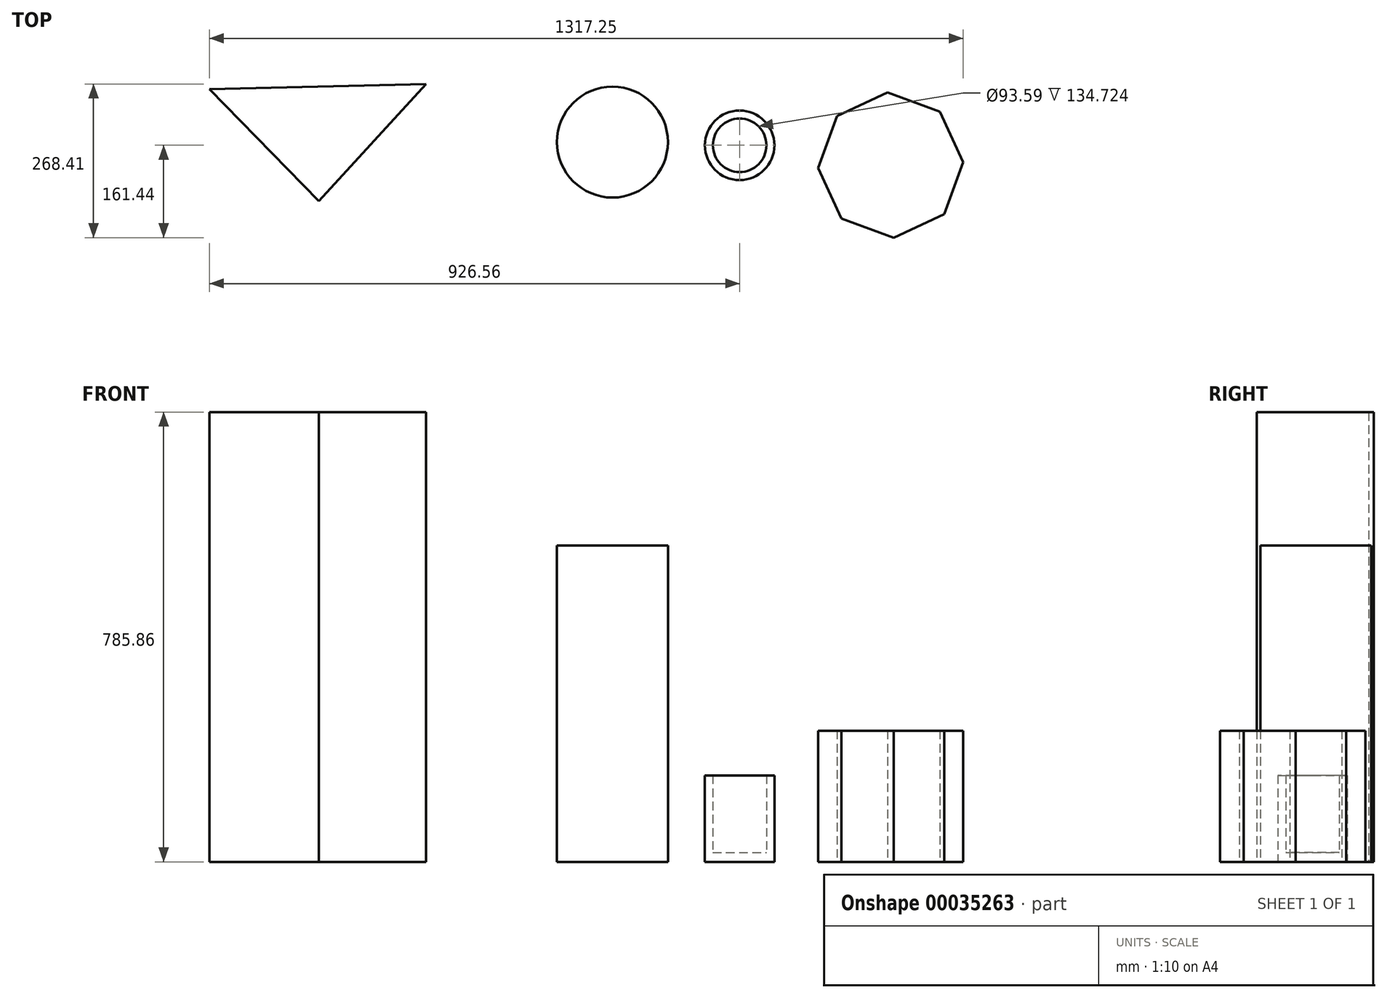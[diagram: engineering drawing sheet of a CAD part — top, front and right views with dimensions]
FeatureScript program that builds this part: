
annotation { "Feature Type Name" : "Feature", "Feature Type Description" : "" }
export const myFeature = defineFeature(function(context is Context, id is Id, definition is map)
    precondition{}
    {
        {
            var Q0;
            Q0=qCreatedBy(makeId("Front.planeOp"),FACE);
            var sketch = newSketch(context, id + "F0", { "sketchPlane" : qUnion([Q0])});
            skLineSegment(sketch, "E0.bottom", {"start": v(0, 0) * mm, "end": v(60.7, 0) * mm});
            skLineSegment(sketch, "E0.top", {"start": v(0, 16.33) * mm, "end": v(60.7, 16.33) * mm});
            skLineSegment(sketch, "E0.left", {"start": v(0, 0) * mm, "end": v(0, 16.33) * mm});
            skLineSegment(sketch, "E0.right", {"start": v(60.7, 0) * mm, "end": v(60.7, 16.33) * mm});
            skLineSegment(sketch, "E1.bottom", {"start": v(60.7, 0) * mm, "end": v(46.8, 0) * mm});
            skLineSegment(sketch, "E1.top", {"start": v(60.7, 151.05) * mm, "end": v(46.8, 151.05) * mm});
            skLineSegment(sketch, "E1.left", {"start": v(60.7, 0) * mm, "end": v(60.7, 151.05) * mm});
            skLineSegment(sketch, "E1.right", {"start": v(46.8, 0) * mm, "end": v(46.8, 151.05) * mm});
            skLineSegment(sketch, "E2", {"start": v(0, 0) * mm, "end": v(0, 193.86) * mm, "construction": true});
            skSolve(sketch);
        }
        {
            var Q0;
            {var subQ5=sQuery(id+"F0.wireOp",EDGE,"E1.top");Q0=makeQuery(id+"F0.imprint","IMPRINT",FACE,{"disambiguationData":[TD([[makeQuery(id+"F0.imprint","IMPRINT",EDGE,{"derivedFrom":subQ5}),1.0]])]});}
            var Q1;
            {var subQ5=sQuery(id+"F0.wireOp",EDGE,"E1.bottom");Q1=makeQuery(id+"F0.imprint","IMPRINT",FACE,{"disambiguationData":[TD([[makeQuery(id+"F0.imprint","IMPRINT",EDGE,{"derivedFrom":subQ5}),-1.0]])]});}
            var Q2;
            {var subQ0=sQuery(id+"F0.wireOp",EDGE,"E0.bottom");Q2=makeQuery(id+"F0.imprint","IMPRINT",FACE,{"disambiguationData":[TD([[makeQuery(id+"F0.imprint","IMPRINT",EDGE,{"derivedFrom":subQ0}),1.0]])]});}
            var Q3;
            Q3=sQuery(id+"F0.wireOp",EDGE,"E2");
            revolve(context, id + "F1", {"entities" : qUnion([Q0, Q1, Q2]), "axis" : qUnion([Q3]), "revolveType" : RevolveType.FULL});
        }
        {
            var Q0;
            Q0=qCreatedBy(makeId("Top.planeOp"),FACE);
            var sketch = newSketch(context, id + "F6", { "sketchPlane" : qUnion([Q0])});
            skCircle(sketch, "E3.cCircle", {"center": v(263.86, -34.6) * mm, "radius": 117.28 * mm, "construction": true});
            skLineSegment(sketch, "E3.0", {"start": v(390.7, -29.3) * mm, "end": v(357.28, -120.55) * mm});
            skLineSegment(sketch, "E3.1", {"start": v(357.28, -120.55) * mm, "end": v(269.15, -161.44) * mm});
            skLineSegment(sketch, "E3.2", {"start": v(269.15, -161.44) * mm, "end": v(177.91, -128.03) * mm});
            skLineSegment(sketch, "E3.3", {"start": v(177.91, -128.03) * mm, "end": v(137.02, -39.9) * mm});
            skLineSegment(sketch, "E3.4", {"start": v(137.02, -39.9) * mm, "end": v(170.43, 51.34) * mm});
            skLineSegment(sketch, "E3.5", {"start": v(170.43, 51.34) * mm, "end": v(258.56, 92.24) * mm});
            skLineSegment(sketch, "E3.6", {"start": v(258.56, 92.24) * mm, "end": v(349.8, 58.83) * mm});
            skLineSegment(sketch, "E3.7", {"start": v(349.8, 58.83) * mm, "end": v(390.7, -29.3) * mm});
            skPoint(sketch, "E3.0.midPoint", {"position": v(373.99, -74.93) * mm});
            skSolve(sketch);
        }
        {
            var Q0;
            Q0=makeQuery(id+"F6.imprint","IMPRINT",FACE,{"disambiguationData":[TD([[makeQuery(id+"F6.imprint","IMPRINT",EDGE,{"derivedFrom":sQuery(id+"F6.wireOp",EDGE,"E3.0")}),-1.0]])]});
            extrude(context, id + "F2", {"entities" : qUnion([Q0]), "depth" : 229.13 * mm});
        }
        {
            var Q0;
            Q0=qCreatedBy(makeId("Top.planeOp"),FACE);
            var sketch = newSketch(context, id + "F3", { "sketchPlane" : qUnion([Q0])});
            skCircle(sketch, "E4", {"center": v(-222.22, 5.56) * mm, "radius": 96.93 * mm});
            skSolve(sketch);
        }
        {
            var Q0;
            Q0=makeQuery(id+"F3.imprint","IMPRINT",FACE,{"disambiguationData":[TD([[makeQuery(id+"F3.imprint","IMPRINT",EDGE,{"derivedFrom":sQuery(id+"F3.wireOp",EDGE,"E4")}),1.0]])]});
            extrude(context, id + "F4", {"entities" : qUnion([Q0]), "depth" : 553.1 * mm});
        }
        {
            var Q0;
            Q0=qCreatedBy(makeId("Top.planeOp"),FACE);
            var sketch = newSketch(context, id + "F5", { "sketchPlane" : qUnion([Q0])});
            skLineSegment(sketch, "E5", {"start": v(-735.43, -97.78) * mm, "end": v(-547.9, 106.97) * mm});
            skLineSegment(sketch, "E6", {"start": v(-547.9, 106.97) * mm, "end": v(-926.56, 97.96) * mm});
            skLineSegment(sketch, "E7", {"start": v(-926.56, 97.96) * mm, "end": v(-735.43, -97.78) * mm});
            skSolve(sketch);
        }
        {
            var Q0;
            Q0=makeQuery(id+"F5.imprint","IMPRINT",FACE,{"disambiguationData":[TD([[makeQuery(id+"F5.imprint","IMPRINT",EDGE,{"derivedFrom":sQuery(id+"F5.wireOp",EDGE,"E5")}),1.0]])]});
            extrude(context, id + "F7", {"entities" : qUnion([Q0]), "depth" : 785.86 * mm});
        }
    });
